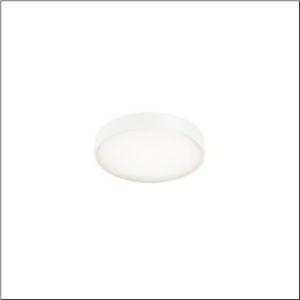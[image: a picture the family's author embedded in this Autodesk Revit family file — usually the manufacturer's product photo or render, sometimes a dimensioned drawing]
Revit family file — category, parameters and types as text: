
# Revit family: round_21_s_51mr34fd0421w
name_source: partatom
category: Lighting Fixtures
units: mm (PartAtom-declared; Revit-internal decimal feet)

## family parameters
Cut with Voids When Loaded = No
Host = Face
Light Source = No
Part Type = Normal
Room Calculation Point = No
Round Connector Dimension = Use Diameter
Shared = No

## types (1)
- Round 21 S (1 x LED, 3910 lm, 30.3 W, 4000K)
    Apparent Load = 30 VA
    CIE Flux Codes = 49 80 96 100 100
    Color Rendering = 80
    Color Temperature = 4000K
    Default Elevation = 1800 mm
    Description = Round 21 S, wall and ceiling luminaire, primary optical cover: cover, of PMMA, opal, light emission: direct distribution, primary light characteristic: symmetric, installation type: suspended mounting, surface-mounted, LED, rated luminous flux: 3.900lm, luminous efficacy: 129lm/W, light colour: 840, colour temperature: 4000K, control gear: DALI 2, with terminal, 5-pole, mains connection: 230V, AC, 50/60Hz, rated input power: 30.3W, housing, of aluminium, coated, white, diameter: 400mm, height: 62mm, protection rating (complete): IP40, insulation class (complete): insulation class I (protective earthing), certification: CE, impact resistance: IK04, permissible operating ambient temperature: -10..+35°C, packaging unit: 1 piece
    Height = 87 mm
    Lamp = 1 x LED
    Lamp Light Flux = 3910 lm
    Lamp Power = 30.3 W
    Lamp count = 1
    Length = 400 mm
    Luminous efficacy = 129 lm/W
    Manufacturer = Siteco
    ModVariant = No
    Model = 51MR34FD0421W
    Mounting Place = Ceiling
    Mounting Type = Surface mounted
    Number of Poles = 1
    OnlyDefault = Yes
    Power Factor = 1
    Product Name = Round 21 S
    Product group = wall and ceiling luminaire | ceiling mounted
    ProductGroupID = 305
    Protection Class = Protection class I
    Protection Degree = IP 40
    RLX_Detail_Level = 1
    RLX_Emergency_Light_Flux = 0 lm
    RLX_Emergency_Type = 0
    RLX_Emergency_Type_DB = No
    RlxData = <blob elided: 9529 chars, md5=5329c840>
    Socket = socket
    Standby Power = 0 W
    System Light Flux = 3910 lm
    System Power = 30 W
    Type Comments = Product without accessories
    Type Image = l_1258307.jpg
    URL = http://relux.com
    VarID = ---
    Voltage = 0 V
    Weight = 0.00 kg
    Width = 0 mm  [stored 0 ft]

note: [stored X ft] marks values corroborated as IEEE doubles in the binary element streams (Revit-internal decimal feet)

## geometry (parser evidence)
native form markers: Sweep x10
no freeform markers — native parametric forms only
